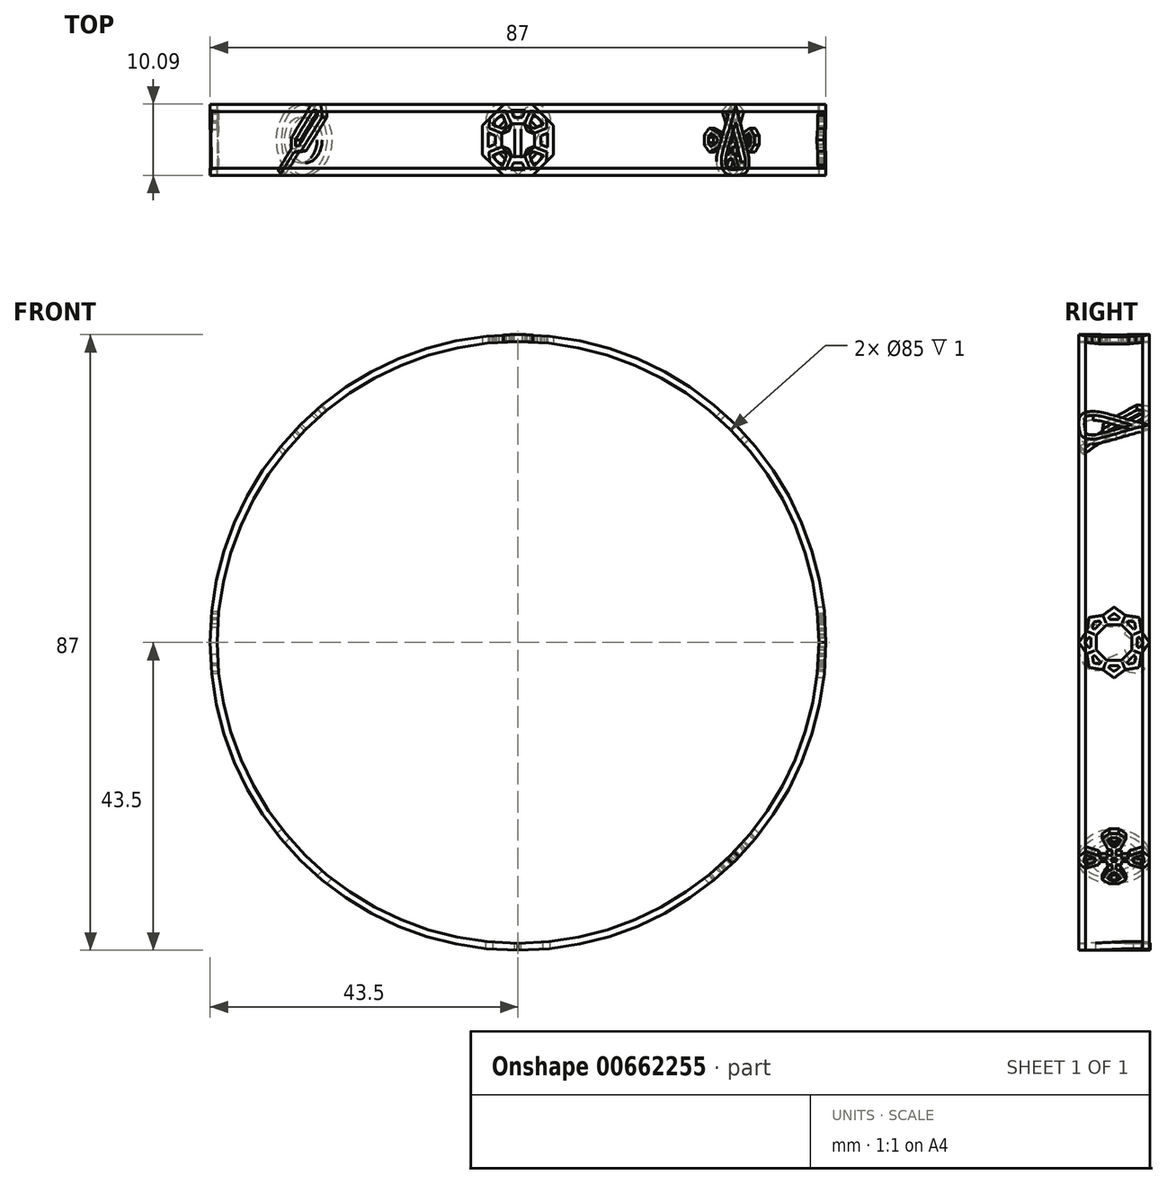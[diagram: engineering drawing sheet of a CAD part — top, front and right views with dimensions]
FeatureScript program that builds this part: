
annotation { "Feature Type Name" : "Feature", "Feature Type Description" : "" }
export const myFeature = defineFeature(function(context is Context, id is Id, definition is map)
    precondition{}
    {
        {
            var Q0;
            Q0=qCreatedBy(makeId("Top.planeOp"),FACE);
            var sketch = newSketch(context, id + "F0", { "sketchPlane" : qUnion([Q0])});
            skCircle(sketch, "E0.cCircle", {"center": v(0, 0) * mm, "radius": 5.41 * mm, "construction": true});
            skLineSegment(sketch, "E0.0", {"start": v(2.07, 5) * mm, "end": v(5, 2.07) * mm});
            skLineSegment(sketch, "E0.1", {"start": v(5, 2.07) * mm, "end": v(5, -2.07) * mm});
            skLineSegment(sketch, "E0.2", {"start": v(5, -2.07) * mm, "end": v(2.07, -5) * mm});
            skLineSegment(sketch, "E0.3", {"start": v(2.07, -5) * mm, "end": v(-2.07, -5) * mm});
            skLineSegment(sketch, "E0.4", {"start": v(-2.07, -5) * mm, "end": v(-5, -2.07) * mm});
            skLineSegment(sketch, "E0.5", {"start": v(-5, -2.07) * mm, "end": v(-5, 2.07) * mm});
            skLineSegment(sketch, "E0.6", {"start": v(-5, 2.07) * mm, "end": v(-2.07, 5) * mm});
            skLineSegment(sketch, "E0.7", {"start": v(-2.07, 5) * mm, "end": v(2.07, 5) * mm});
            skCircle(sketch, "E1.cCircle", {"center": v(0, 0) * mm, "radius": 2.88 * mm, "construction": true});
            skLineSegment(sketch, "E1.0", {"start": v(1.1, 2.66) * mm, "end": v(2.66, 1.1) * mm});
            skLineSegment(sketch, "E1.1", {"start": v(2.66, 1.1) * mm, "end": v(2.66, -1.1) * mm});
            skLineSegment(sketch, "E1.2", {"start": v(2.66, -1.1) * mm, "end": v(1.1, -2.66) * mm});
            skLineSegment(sketch, "E1.3", {"start": v(1.1, -2.66) * mm, "end": v(-1.1, -2.66) * mm});
            skLineSegment(sketch, "E1.4", {"start": v(-1.1, -2.66) * mm, "end": v(-2.66, -1.1) * mm});
            skLineSegment(sketch, "E1.5", {"start": v(-2.66, -1.1) * mm, "end": v(-2.66, 1.1) * mm});
            skLineSegment(sketch, "E1.6", {"start": v(-2.66, 1.1) * mm, "end": v(-1.1, 2.66) * mm});
            skLineSegment(sketch, "E1.7", {"start": v(-1.1, 2.66) * mm, "end": v(1.1, 2.66) * mm});
            skLineSegment(sketch, "E2", {"start": v(-2.07, 5) * mm, "end": v(-1.1, 2.66) * mm});
            skLineSegment(sketch, "E3", {"start": v(-2.66, 1.1) * mm, "end": v(-5, 2.07) * mm});
            skLineSegment(sketch, "E4", {"start": v(-5, -2.07) * mm, "end": v(-2.66, -1.1) * mm});
            skLineSegment(sketch, "E5", {"start": v(-1.1, -2.66) * mm, "end": v(-2.07, -5) * mm});
            skLineSegment(sketch, "E6", {"start": v(1.1, -2.66) * mm, "end": v(2.07, -5) * mm});
            skLineSegment(sketch, "E7", {"start": v(5, -2.07) * mm, "end": v(2.66, -1.1) * mm});
            skLineSegment(sketch, "E8", {"start": v(2.66, 1.1) * mm, "end": v(5, 2.07) * mm});
            skLineSegment(sketch, "E9", {"start": v(2.07, 5) * mm, "end": v(1.1, 2.66) * mm});
            skLineSegment(sketch, "E10", {"start": v(1.03, 4.18) * mm, "end": v(0.62, 3.2) * mm});
            skLineSegment(sketch, "E11", {"start": v(0.62, 3.2) * mm, "end": v(-0.58, 3.2) * mm});
            skLineSegment(sketch, "E12", {"start": v(-0.58, 3.2) * mm, "end": v(-0.98, 4.18) * mm});
            skLineSegment(sketch, "E13", {"start": v(-0.98, 4.18) * mm, "end": v(1.03, 4.18) * mm});
            skLineSegment(sketch, "E14.MirrorCS", {"start": v(2.23, 3.68) * mm, "end": v(1.82, 2.7) * mm});
            skLineSegment(sketch, "E15.MirrorCS", {"start": v(3.65, 2.26) * mm, "end": v(2.23, 3.68) * mm});
            skLineSegment(sketch, "E16.MirrorCS", {"start": v(1.82, 2.7) * mm, "end": v(2.67, 1.85) * mm});
            skLineSegment(sketch, "E17.MirrorCS", {"start": v(2.67, 1.85) * mm, "end": v(3.65, 2.26) * mm});
            skLineSegment(sketch, "E18.MirrorCS", {"start": v(3.2, 0.58) * mm, "end": v(4.18, 0.98) * mm});
            skLineSegment(sketch, "E19.MirrorCS", {"start": v(3.2, -0.62) * mm, "end": v(3.2, 0.58) * mm});
            skLineSegment(sketch, "E20.MirrorCS", {"start": v(4.18, -1.03) * mm, "end": v(3.2, -0.62) * mm});
            skLineSegment(sketch, "E21.MirrorCS", {"start": v(4.18, 0.98) * mm, "end": v(4.18, -1.03) * mm});
            skLineSegment(sketch, "E22.MirrorCS", {"start": v(5, -2.07) * mm, "end": v(5, 2.07) * mm});
            skLineSegment(sketch, "E23.MirrorCS", {"start": v(3.68, -2.23) * mm, "end": v(2.7, -1.82) * mm});
            skLineSegment(sketch, "E24.MirrorCS", {"start": v(2.7, -1.82) * mm, "end": v(1.85, -2.67) * mm});
            skLineSegment(sketch, "E25.MirrorCS", {"start": v(1.85, -2.67) * mm, "end": v(2.26, -3.65) * mm});
            skLineSegment(sketch, "E26.MirrorCS", {"start": v(2.26, -3.65) * mm, "end": v(3.68, -2.23) * mm});
            skLineSegment(sketch, "E27.MirrorCS", {"start": v(0.58, -3.2) * mm, "end": v(0.98, -4.18) * mm});
            skLineSegment(sketch, "E28.MirrorCS", {"start": v(-0.62, -3.2) * mm, "end": v(0.58, -3.2) * mm});
            skLineSegment(sketch, "E29.MirrorCS", {"start": v(0.98, -4.18) * mm, "end": v(-1.03, -4.18) * mm});
            skLineSegment(sketch, "E30.MirrorCS", {"start": v(-1.03, -4.18) * mm, "end": v(-0.62, -3.2) * mm});
            skLineSegment(sketch, "E31.MirrorCS", {"start": v(-2.23, -3.68) * mm, "end": v(-1.82, -2.7) * mm});
            skLineSegment(sketch, "E32.MirrorCS", {"start": v(-1.82, -2.7) * mm, "end": v(-2.67, -1.85) * mm});
            skLineSegment(sketch, "E33.MirrorCS", {"start": v(-2.67, -1.85) * mm, "end": v(-3.65, -2.26) * mm});
            skLineSegment(sketch, "E34.MirrorCS", {"start": v(-3.65, -2.26) * mm, "end": v(-2.23, -3.68) * mm});
            skLineSegment(sketch, "E35.MirrorCS", {"start": v(-3.2, -0.58) * mm, "end": v(-4.18, -0.98) * mm});
            skLineSegment(sketch, "E36.MirrorCS", {"start": v(-2.66, -1.1) * mm, "end": v(-1.1, -2.66) * mm});
            skLineSegment(sketch, "E37.MirrorCS", {"start": v(-3.2, 0.62) * mm, "end": v(-3.2, -0.58) * mm});
            skLineSegment(sketch, "E38.MirrorCS", {"start": v(-4.18, -0.98) * mm, "end": v(-4.18, 1.03) * mm});
            skLineSegment(sketch, "E39.MirrorCS", {"start": v(-4.18, 1.03) * mm, "end": v(-3.2, 0.62) * mm});
            skLineSegment(sketch, "E40.MirrorCS", {"start": v(-3.68, 2.23) * mm, "end": v(-2.7, 1.82) * mm});
            skLineSegment(sketch, "E41.MirrorCS", {"start": v(-2.7, 1.82) * mm, "end": v(-1.85, 2.67) * mm});
            skLineSegment(sketch, "E42.MirrorCS", {"start": v(-1.85, 2.67) * mm, "end": v(-2.26, 3.65) * mm});
            skLineSegment(sketch, "E43.MirrorCS", {"start": v(-2.26, 3.65) * mm, "end": v(-3.68, 2.23) * mm});
            skCircle(sketch, "E44.cCircle", {"center": v(0, 0) * mm, "radius": 2.5 * mm, "construction": true});
            skLineSegment(sketch, "E44.0", {"start": v(0.96, 2.3) * mm, "end": v(2.3, 0.96) * mm});
            skLineSegment(sketch, "E44.1", {"start": v(2.3, 0.96) * mm, "end": v(2.3, -0.96) * mm});
            skLineSegment(sketch, "E44.2", {"start": v(2.3, -0.96) * mm, "end": v(0.96, -2.3) * mm});
            skLineSegment(sketch, "E44.3", {"start": v(0.96, -2.3) * mm, "end": v(-0.96, -2.3) * mm});
            skLineSegment(sketch, "E44.4", {"start": v(-0.96, -2.3) * mm, "end": v(-2.3, -0.96) * mm});
            skLineSegment(sketch, "E44.5", {"start": v(-2.3, -0.96) * mm, "end": v(-2.3, 0.96) * mm});
            skLineSegment(sketch, "E44.6", {"start": v(-2.3, 0.96) * mm, "end": v(-0.96, 2.3) * mm});
            skLineSegment(sketch, "E44.7", {"start": v(-0.96, 2.3) * mm, "end": v(0.96, 2.3) * mm});
            skSolve(sketch);
        }
        {
            var Q0;
            Q0=qCreatedBy(makeId("Top.planeOp"),FACE);
            var sketch = newSketch(context, id + "F1", { "sketchPlane" : qUnion([Q0])});
            skPoint(sketch, "E45", {"position": v(0, 5) * mm});
            skPoint(sketch, "E46", {"position": v(0.02, -5) * mm});
            skFitSpline(sketch, "E47", {"points": [v(0, 5) * mm, v(-2.77, -3.02) * mm], "startDerivative": vector(-3.23, -10.51) * mm, "endDerivative": vector(0.27, -4.22) * mm});
            skFitSpline(sketch, "E48", {"points": [v(-2.77, -3.02) * mm, v(0.02, -5) * mm], "startDerivative": vector(0.37, -5.85) * mm, "endDerivative": vector(4.25, -0.07) * mm});
            skFitSpline(sketch, "E49.MirrorCS", {"points": [v(0, 5) * mm, v(2.77, -3.16) * mm], "startDerivative": vector(3.23, -10.51) * mm, "endDerivative": vector(-0.27, -4.22) * mm});
            skFitSpline(sketch, "E50.MirrorCS", {"points": [v(2.77, -3.16) * mm, v(-0.03, -5) * mm], "startDerivative": vector(-0.37, -5.82) * mm, "endDerivative": vector(-4.2, -0.7) * mm});
            skFitSpline(sketch, "E51.0", {"points": [v(-0.76, 4.76) * mm, v(-0.49, 3.86) * mm, v(0.15, 2.1) * mm, v(0.96, 0.15) * mm, v(1.48, -1.19) * mm, v(1.78, -2.05) * mm, v(1.96, -2.74) * mm, v(1.98, -3.03) * mm, v(1.97, -3.11) * mm]});
            skFitSpline(sketch, "E51.1", {"points": [v(0.76, 4.76) * mm, v(0.49, 3.86) * mm, v(-0.15, 2.12) * mm, v(-0.96, 0.2) * mm, v(-1.48, -1.1) * mm, v(-1.78, -1.94) * mm, v(-1.96, -2.6) * mm, v(-1.98, -2.9) * mm, v(-1.97, -2.97) * mm]});
            skFitSpline(sketch, "E51.2", {"points": [v(-1.97, -2.97) * mm, v(-1.96, -3.18) * mm, v(-1.9, -3.5) * mm, v(-1.79, -3.78) * mm, v(-1.67, -3.92) * mm, v(-1.52, -4.02) * mm, v(-1.28, -4.1) * mm, v(-0.92, -4.16) * mm, v(-0.48, -4.2) * mm, v(-0.14, -4.2) * mm, v(0.04, -4.2) * mm]});
            skFitSpline(sketch, "E51.3", {"points": [v(1.97, -3.11) * mm, v(1.96, -3.31) * mm, v(1.9, -3.62) * mm, v(1.8, -3.83) * mm, v(1.73, -3.9) * mm, v(1.6, -3.98) * mm, v(1.32, -4.05) * mm, v(0.92, -4.1) * mm, v(0.42, -4.14) * mm, v(0.04, -4.18) * mm, v(-0.16, -4.22) * mm]});
            skSolve(sketch);
        }
        {
            var Q0;
            Q0=qCreatedBy(makeId("Top.planeOp"),FACE);
            var sketch = newSketch(context, id + "F2", { "sketchPlane" : qUnion([Q0])});
            skCircle(sketch, "E52.cCircle", {"center": v(0, 0) * mm, "radius": 3 * mm, "construction": true});
            skLineSegment(sketch, "E52.0", {"start": v(1.15, 2.77) * mm, "end": v(2.77, 1.15) * mm});
            skLineSegment(sketch, "E52.1", {"start": v(2.77, 1.15) * mm, "end": v(2.77, -1.15) * mm});
            skLineSegment(sketch, "E52.2", {"start": v(2.77, -1.15) * mm, "end": v(1.15, -2.77) * mm});
            skLineSegment(sketch, "E52.3", {"start": v(1.15, -2.77) * mm, "end": v(-1.15, -2.77) * mm});
            skLineSegment(sketch, "E52.4", {"start": v(-1.15, -2.77) * mm, "end": v(-2.77, -1.15) * mm});
            skLineSegment(sketch, "E52.5", {"start": v(-2.77, -1.15) * mm, "end": v(-2.77, 1.15) * mm});
            skLineSegment(sketch, "E52.6", {"start": v(-2.77, 1.15) * mm, "end": v(-1.15, 2.77) * mm});
            skLineSegment(sketch, "E52.7", {"start": v(-1.15, 2.77) * mm, "end": v(1.15, 2.77) * mm});
            skLineSegment(sketch, "E53", {"start": v(-1.15, 2.77) * mm, "end": v(-1.58, 3.85) * mm});
            skLineSegment(sketch, "E54", {"start": v(-1.58, 3.85) * mm, "end": v(0, 5) * mm});
            skLineSegment(sketch, "E55.MirrorCS", {"start": v(1.58, 3.85) * mm, "end": v(0, 5) * mm});
            skLineSegment(sketch, "E56.MirrorCS", {"start": v(1.15, 2.77) * mm, "end": v(1.58, 3.85) * mm});
            skLineSegment(sketch, "E57.1.0", {"start": v(-1.15, 2.77) * mm, "end": v(-1.6, 3.84) * mm});
            skLineSegment(sketch, "E57.1.1", {"start": v(-1.6, 3.84) * mm, "end": v(-3.54, 3.54) * mm});
            skLineSegment(sketch, "E57.1.2", {"start": v(-3.84, 1.6) * mm, "end": v(-3.54, 3.54) * mm});
            skLineSegment(sketch, "E57.1.3", {"start": v(-2.77, 1.15) * mm, "end": v(-3.84, 1.6) * mm});
            skLineSegment(sketch, "E57.2.0", {"start": v(-2.77, 1.15) * mm, "end": v(-3.85, 1.58) * mm});
            skLineSegment(sketch, "E57.2.1", {"start": v(-3.85, 1.58) * mm, "end": v(-5, 0) * mm});
            skLineSegment(sketch, "E57.2.2", {"start": v(-3.85, -1.58) * mm, "end": v(-5, 0) * mm});
            skLineSegment(sketch, "E57.2.3", {"start": v(-2.77, -1.15) * mm, "end": v(-3.85, -1.58) * mm});
            skLineSegment(sketch, "E57.3.0", {"start": v(-2.77, -1.15) * mm, "end": v(-3.84, -1.6) * mm});
            skLineSegment(sketch, "E57.3.1", {"start": v(-3.84, -1.6) * mm, "end": v(-3.54, -3.54) * mm});
            skLineSegment(sketch, "E57.3.2", {"start": v(-1.6, -3.84) * mm, "end": v(-3.54, -3.54) * mm});
            skLineSegment(sketch, "E57.3.3", {"start": v(-1.15, -2.77) * mm, "end": v(-1.6, -3.84) * mm});
            skLineSegment(sketch, "E57.4.0", {"start": v(-1.15, -2.77) * mm, "end": v(-1.58, -3.85) * mm});
            skLineSegment(sketch, "E57.4.1", {"start": v(-1.58, -3.85) * mm, "end": v(0, -5) * mm});
            skLineSegment(sketch, "E57.4.2", {"start": v(1.58, -3.85) * mm, "end": v(0, -5) * mm});
            skLineSegment(sketch, "E57.4.3", {"start": v(1.15, -2.77) * mm, "end": v(1.58, -3.85) * mm});
            skLineSegment(sketch, "E57.5.0", {"start": v(1.15, -2.77) * mm, "end": v(1.6, -3.84) * mm});
            skLineSegment(sketch, "E57.5.1", {"start": v(1.6, -3.84) * mm, "end": v(3.54, -3.54) * mm});
            skLineSegment(sketch, "E57.5.2", {"start": v(3.84, -1.6) * mm, "end": v(3.54, -3.54) * mm});
            skLineSegment(sketch, "E57.5.3", {"start": v(2.77, -1.15) * mm, "end": v(3.84, -1.6) * mm});
            skLineSegment(sketch, "E57.6.0", {"start": v(2.77, -1.15) * mm, "end": v(3.85, -1.58) * mm});
            skLineSegment(sketch, "E57.6.1", {"start": v(3.85, -1.58) * mm, "end": v(5, 0) * mm});
            skLineSegment(sketch, "E57.6.2", {"start": v(3.85, 1.58) * mm, "end": v(5, 0) * mm});
            skLineSegment(sketch, "E57.6.3", {"start": v(2.77, 1.15) * mm, "end": v(3.85, 1.58) * mm});
            skLineSegment(sketch, "E57.7.0", {"start": v(2.77, 1.15) * mm, "end": v(3.84, 1.6) * mm});
            skLineSegment(sketch, "E57.7.1", {"start": v(3.84, 1.6) * mm, "end": v(3.54, 3.54) * mm});
            skLineSegment(sketch, "E57.7.2", {"start": v(1.6, 3.84) * mm, "end": v(3.54, 3.54) * mm});
            skLineSegment(sketch, "E57.7.3", {"start": v(1.15, 2.77) * mm, "end": v(1.6, 3.84) * mm});
            skLineSegment(sketch, "E58", {"start": v(0, 4.1) * mm, "end": v(-0.73, 3.56) * mm});
            skLineSegment(sketch, "E59", {"start": v(-0.73, 3.56) * mm, "end": v(-0.61, 3.26) * mm});
            skLineSegment(sketch, "E60", {"start": v(-0.61, 3.26) * mm, "end": v(0.62, 3.26) * mm});
            skLineSegment(sketch, "E61", {"start": v(0.62, 3.26) * mm, "end": v(0.74, 3.56) * mm});
            skLineSegment(sketch, "E62", {"start": v(0.74, 3.56) * mm, "end": v(0, 4.1) * mm});
            skCircle(sketch, "E63.cCircle", {"center": v(0, 0) * mm, "radius": 2.73 * mm, "construction": true});
            skLineSegment(sketch, "E63.0", {"start": v(1.05, 2.52) * mm, "end": v(2.52, 1.05) * mm});
            skLineSegment(sketch, "E63.1", {"start": v(2.52, 1.05) * mm, "end": v(2.52, -1.05) * mm});
            skLineSegment(sketch, "E63.2", {"start": v(2.52, -1.05) * mm, "end": v(1.05, -2.52) * mm});
            skLineSegment(sketch, "E63.3", {"start": v(1.05, -2.52) * mm, "end": v(-1.05, -2.52) * mm});
            skLineSegment(sketch, "E63.4", {"start": v(-1.05, -2.52) * mm, "end": v(-2.52, -1.05) * mm});
            skLineSegment(sketch, "E63.5", {"start": v(-2.52, -1.05) * mm, "end": v(-2.52, 1.05) * mm});
            skLineSegment(sketch, "E63.6", {"start": v(-2.52, 1.05) * mm, "end": v(-1.05, 2.52) * mm});
            skLineSegment(sketch, "E63.7", {"start": v(-1.05, 2.52) * mm, "end": v(1.05, 2.52) * mm});
            skLineSegment(sketch, "E64.1.1", {"start": v(-1.87, 2.74) * mm, "end": v(-2, 3.04) * mm});
            skLineSegment(sketch, "E64.1.2", {"start": v(-2.74, 1.87) * mm, "end": v(-1.87, 2.74) * mm});
            skLineSegment(sketch, "E64.1.3", {"start": v(-3.04, 2) * mm, "end": v(-2.74, 1.87) * mm});
            skLineSegment(sketch, "E64.1.4", {"start": v(-2.9, 2.9) * mm, "end": v(-3.04, 2) * mm});
            skLineSegment(sketch, "E64.1.5", {"start": v(-2, 3.04) * mm, "end": v(-2.9, 2.9) * mm});
            skLineSegment(sketch, "E64.2.1", {"start": v(-3.26, 0.62) * mm, "end": v(-3.56, 0.74) * mm});
            skLineSegment(sketch, "E64.2.2", {"start": v(-3.26, -0.61) * mm, "end": v(-3.26, 0.62) * mm});
            skLineSegment(sketch, "E64.2.3", {"start": v(-3.56, -0.73) * mm, "end": v(-3.26, -0.61) * mm});
            skLineSegment(sketch, "E64.2.4", {"start": v(-4.1, 0) * mm, "end": v(-3.56, -0.73) * mm});
            skLineSegment(sketch, "E64.2.5", {"start": v(-3.56, 0.74) * mm, "end": v(-4.1, 0) * mm});
            skLineSegment(sketch, "E64.3.1", {"start": v(-2.74, -1.87) * mm, "end": v(-3.04, -2) * mm});
            skLineSegment(sketch, "E64.3.2", {"start": v(-1.87, -2.74) * mm, "end": v(-2.74, -1.87) * mm});
            skLineSegment(sketch, "E64.3.3", {"start": v(-2, -3.04) * mm, "end": v(-1.87, -2.74) * mm});
            skLineSegment(sketch, "E64.3.4", {"start": v(-2.9, -2.9) * mm, "end": v(-2, -3.04) * mm});
            skLineSegment(sketch, "E64.3.5", {"start": v(-3.04, -2) * mm, "end": v(-2.9, -2.9) * mm});
            skLineSegment(sketch, "E64.4.1", {"start": v(-0.62, -3.26) * mm, "end": v(-0.74, -3.56) * mm});
            skLineSegment(sketch, "E64.4.2", {"start": v(0.61, -3.26) * mm, "end": v(-0.62, -3.26) * mm});
            skLineSegment(sketch, "E64.4.3", {"start": v(0.73, -3.56) * mm, "end": v(0.61, -3.26) * mm});
            skLineSegment(sketch, "E64.4.4", {"start": v(0, -4.1) * mm, "end": v(0.73, -3.56) * mm});
            skLineSegment(sketch, "E64.4.5", {"start": v(-0.74, -3.56) * mm, "end": v(0, -4.1) * mm});
            skLineSegment(sketch, "E64.5.1", {"start": v(1.87, -2.74) * mm, "end": v(2, -3.04) * mm});
            skLineSegment(sketch, "E64.5.2", {"start": v(2.74, -1.87) * mm, "end": v(1.87, -2.74) * mm});
            skLineSegment(sketch, "E64.5.3", {"start": v(3.04, -2) * mm, "end": v(2.74, -1.87) * mm});
            skLineSegment(sketch, "E64.5.4", {"start": v(2.9, -2.9) * mm, "end": v(3.04, -2) * mm});
            skLineSegment(sketch, "E64.5.5", {"start": v(2, -3.04) * mm, "end": v(2.9, -2.9) * mm});
            skLineSegment(sketch, "E64.6.1", {"start": v(3.26, -0.62) * mm, "end": v(3.56, -0.74) * mm});
            skLineSegment(sketch, "E64.6.2", {"start": v(3.26, 0.61) * mm, "end": v(3.26, -0.62) * mm});
            skLineSegment(sketch, "E64.6.3", {"start": v(3.56, 0.73) * mm, "end": v(3.26, 0.61) * mm});
            skLineSegment(sketch, "E64.6.4", {"start": v(4.1, 0) * mm, "end": v(3.56, 0.73) * mm});
            skLineSegment(sketch, "E64.6.5", {"start": v(3.56, -0.74) * mm, "end": v(4.1, 0) * mm});
            skLineSegment(sketch, "E64.7.1", {"start": v(2.74, 1.87) * mm, "end": v(3.04, 2) * mm});
            skLineSegment(sketch, "E64.7.2", {"start": v(1.87, 2.74) * mm, "end": v(2.74, 1.87) * mm});
            skLineSegment(sketch, "E64.7.3", {"start": v(2, 3.04) * mm, "end": v(1.87, 2.74) * mm});
            skLineSegment(sketch, "E64.7.4", {"start": v(2.9, 2.9) * mm, "end": v(2, 3.04) * mm});
            skLineSegment(sketch, "E64.7.5", {"start": v(3.04, 2) * mm, "end": v(2.9, 2.9) * mm});
            skSolve(sketch);
        }
        {
            var Q0;
            Q0=qCreatedBy(makeId("Top.planeOp"),FACE);
            var sketch = newSketch(context, id + "F3", { "sketchPlane" : qUnion([Q0])});
            skLineSegment(sketch, "E65", {"start": v(0.02, 1.79) * mm, "end": v(-0.9, 2.18) * mm});
            skLineSegment(sketch, "E66", {"start": v(-0.9, 2.18) * mm, "end": v(-1.7, 4.1) * mm});
            skLineSegment(sketch, "E67", {"start": v(-1.7, 4.1) * mm, "end": v(-0.65, 5) * mm});
            skLineSegment(sketch, "E68", {"start": v(-0.65, 5) * mm, "end": v(0, 5) * mm});
            skLineSegment(sketch, "E69.MirrorCS", {"start": v(0.65, 5) * mm, "end": v(0, 5) * mm});
            skLineSegment(sketch, "E70.MirrorCS", {"start": v(1.7, 4.1) * mm, "end": v(0.65, 5) * mm});
            skLineSegment(sketch, "E71.MirrorCS", {"start": v(0.9, 2.18) * mm, "end": v(1.7, 4.1) * mm});
            skLineSegment(sketch, "E72.MirrorCS", {"start": v(-0.02, 1.79) * mm, "end": v(0.9, 2.18) * mm});
            skLineSegment(sketch, "E73.1.0", {"start": v(-2.18, 0.9) * mm, "end": v(-4.09, 1.7) * mm});
            skLineSegment(sketch, "E73.1.1", {"start": v(-4.09, 1.7) * mm, "end": v(-4, 3.07) * mm});
            skLineSegment(sketch, "E73.1.2", {"start": v(-4, 3.07) * mm, "end": v(-3.54, 3.54) * mm});
            skLineSegment(sketch, "E73.1.3", {"start": v(-1.25, 1.28) * mm, "end": v(-2.18, 0.9) * mm});
            skLineSegment(sketch, "E73.1.4", {"start": v(-3.07, 4) * mm, "end": v(-3.54, 3.54) * mm});
            skLineSegment(sketch, "E73.1.5", {"start": v(-1.7, 4.09) * mm, "end": v(-3.07, 4) * mm});
            skLineSegment(sketch, "E73.1.6", {"start": v(-0.9, 2.18) * mm, "end": v(-1.7, 4.09) * mm});
            skLineSegment(sketch, "E73.1.7", {"start": v(-1.28, 1.25) * mm, "end": v(-0.9, 2.18) * mm});
            skLineSegment(sketch, "E73.2.0", {"start": v(-2.18, -0.9) * mm, "end": v(-4.1, -1.7) * mm});
            skLineSegment(sketch, "E73.2.1", {"start": v(-4.1, -1.7) * mm, "end": v(-5, -0.65) * mm});
            skLineSegment(sketch, "E73.2.2", {"start": v(-5, -0.65) * mm, "end": v(-5, 0) * mm});
            skLineSegment(sketch, "E73.2.3", {"start": v(-1.79, 0.02) * mm, "end": v(-2.18, -0.9) * mm});
            skLineSegment(sketch, "E73.2.4", {"start": v(-5, 0.65) * mm, "end": v(-5, 0) * mm});
            skLineSegment(sketch, "E73.2.5", {"start": v(-4.1, 1.7) * mm, "end": v(-5, 0.65) * mm});
            skLineSegment(sketch, "E73.2.6", {"start": v(-2.18, 0.9) * mm, "end": v(-4.1, 1.7) * mm});
            skLineSegment(sketch, "E73.2.7", {"start": v(-1.79, -0.02) * mm, "end": v(-2.18, 0.9) * mm});
            skLineSegment(sketch, "E73.3.0", {"start": v(-0.9, -2.18) * mm, "end": v(-1.7, -4.09) * mm});
            skLineSegment(sketch, "E73.3.1", {"start": v(-1.7, -4.09) * mm, "end": v(-3.07, -4) * mm});
            skLineSegment(sketch, "E73.3.2", {"start": v(-3.07, -4) * mm, "end": v(-3.54, -3.54) * mm});
            skLineSegment(sketch, "E73.3.3", {"start": v(-1.28, -1.25) * mm, "end": v(-0.9, -2.18) * mm});
            skLineSegment(sketch, "E73.3.4", {"start": v(-4, -3.07) * mm, "end": v(-3.54, -3.54) * mm});
            skLineSegment(sketch, "E73.3.5", {"start": v(-4.09, -1.7) * mm, "end": v(-4, -3.07) * mm});
            skLineSegment(sketch, "E73.3.6", {"start": v(-2.18, -0.9) * mm, "end": v(-4.09, -1.7) * mm});
            skLineSegment(sketch, "E73.3.7", {"start": v(-1.25, -1.28) * mm, "end": v(-2.18, -0.9) * mm});
            skLineSegment(sketch, "E73.4.0", {"start": v(0.9, -2.18) * mm, "end": v(1.7, -4.1) * mm});
            skLineSegment(sketch, "E73.4.1", {"start": v(1.7, -4.1) * mm, "end": v(0.65, -5) * mm});
            skLineSegment(sketch, "E73.4.2", {"start": v(0.65, -5) * mm, "end": v(0, -5) * mm});
            skLineSegment(sketch, "E73.4.3", {"start": v(-0.02, -1.79) * mm, "end": v(0.9, -2.18) * mm});
            skLineSegment(sketch, "E73.4.4", {"start": v(-0.65, -5) * mm, "end": v(0, -5) * mm});
            skLineSegment(sketch, "E73.4.5", {"start": v(-1.7, -4.1) * mm, "end": v(-0.65, -5) * mm});
            skLineSegment(sketch, "E73.4.6", {"start": v(-0.9, -2.18) * mm, "end": v(-1.7, -4.1) * mm});
            skLineSegment(sketch, "E73.4.7", {"start": v(0.02, -1.79) * mm, "end": v(-0.9, -2.18) * mm});
            skLineSegment(sketch, "E73.5.0", {"start": v(2.18, -0.9) * mm, "end": v(4.09, -1.7) * mm});
            skLineSegment(sketch, "E73.5.1", {"start": v(4.09, -1.7) * mm, "end": v(4, -3.07) * mm});
            skLineSegment(sketch, "E73.5.2", {"start": v(4, -3.07) * mm, "end": v(3.54, -3.54) * mm});
            skLineSegment(sketch, "E73.5.3", {"start": v(1.25, -1.28) * mm, "end": v(2.18, -0.9) * mm});
            skLineSegment(sketch, "E73.5.4", {"start": v(3.07, -4) * mm, "end": v(3.54, -3.54) * mm});
            skLineSegment(sketch, "E73.5.5", {"start": v(1.7, -4.09) * mm, "end": v(3.07, -4) * mm});
            skLineSegment(sketch, "E73.5.6", {"start": v(0.9, -2.18) * mm, "end": v(1.7, -4.09) * mm});
            skLineSegment(sketch, "E73.5.7", {"start": v(1.28, -1.25) * mm, "end": v(0.9, -2.18) * mm});
            skLineSegment(sketch, "E73.6.0", {"start": v(2.18, 0.9) * mm, "end": v(4.1, 1.7) * mm});
            skLineSegment(sketch, "E73.6.1", {"start": v(4.1, 1.7) * mm, "end": v(5, 0.65) * mm});
            skLineSegment(sketch, "E73.6.2", {"start": v(5, 0.65) * mm, "end": v(5, 0) * mm});
            skLineSegment(sketch, "E73.6.3", {"start": v(1.79, -0.02) * mm, "end": v(2.18, 0.9) * mm});
            skLineSegment(sketch, "E73.6.4", {"start": v(5, -0.65) * mm, "end": v(5, 0) * mm});
            skLineSegment(sketch, "E73.6.5", {"start": v(4.1, -1.7) * mm, "end": v(5, -0.65) * mm});
            skLineSegment(sketch, "E73.6.6", {"start": v(2.18, -0.9) * mm, "end": v(4.1, -1.7) * mm});
            skLineSegment(sketch, "E73.6.7", {"start": v(1.79, 0.02) * mm, "end": v(2.18, -0.9) * mm});
            skLineSegment(sketch, "E73.7.0", {"start": v(0.9, 2.18) * mm, "end": v(1.7, 4.09) * mm});
            skLineSegment(sketch, "E73.7.1", {"start": v(1.7, 4.09) * mm, "end": v(3.07, 4) * mm});
            skLineSegment(sketch, "E73.7.2", {"start": v(3.07, 4) * mm, "end": v(3.54, 3.54) * mm});
            skLineSegment(sketch, "E73.7.3", {"start": v(1.28, 1.25) * mm, "end": v(0.9, 2.18) * mm});
            skLineSegment(sketch, "E73.7.4", {"start": v(4, 3.07) * mm, "end": v(3.54, 3.54) * mm});
            skLineSegment(sketch, "E73.7.5", {"start": v(4.09, 1.7) * mm, "end": v(4, 3.07) * mm});
            skLineSegment(sketch, "E73.7.6", {"start": v(2.18, 0.9) * mm, "end": v(4.09, 1.7) * mm});
            skLineSegment(sketch, "E73.7.7", {"start": v(1.25, 1.28) * mm, "end": v(2.18, 0.9) * mm});
            skPoint(sketch, "E73.center", {"position": v(0, 0) * mm});
            skLineSegment(sketch, "E74.anchor1", {"start": v(0, 0) * mm, "end": v(0.78, 2.7) * mm, "construction": true});
            skLineSegment(sketch, "E74.anchor2", {"start": v(0, 0) * mm, "end": v(-1.35, 2.46) * mm, "construction": true});
            skLineSegment(sketch, "E75.bottom", {"start": v(0.97, 1.02) * mm, "end": v(-0.97, 1.02) * mm});
            skLineSegment(sketch, "E75.top", {"start": v(0.97, -1.02) * mm, "end": v(-0.97, -1.02) * mm});
            skLineSegment(sketch, "E75.left", {"start": v(0.97, 1.02) * mm, "end": v(0.97, -1.02) * mm});
            skLineSegment(sketch, "E75.right", {"start": v(-0.97, 1.02) * mm, "end": v(-0.97, -1.02) * mm});
            skLineSegment(sketch, "E76", {"start": v(-0.3, 1.93) * mm, "end": v(-0.3, 1.02) * mm});
            skLineSegment(sketch, "E77", {"start": v(0.3, 1.93) * mm, "end": v(0.3, 1.02) * mm});
            skLineSegment(sketch, "E78", {"start": v(0.3, 1.02) * mm, "end": v(0.32, 0.96) * mm});
            skLineSegment(sketch, "E79.MirrorCS", {"start": v(0.3, -1.93) * mm, "end": v(0.3, -1.02) * mm});
            skLineSegment(sketch, "E80.MirrorCS", {"start": v(-0.3, -1.93) * mm, "end": v(-0.3, -1.02) * mm});
            skLineSegment(sketch, "E81", {"start": v(-0.97, 0.3) * mm, "end": v(-1.93, 0.3) * mm});
            skLineSegment(sketch, "E82", {"start": v(-0.97, -0.3) * mm, "end": v(-1.93, -0.3) * mm});
            skLineSegment(sketch, "E83.MirrorCS", {"start": v(0.97, 0.3) * mm, "end": v(1.93, 0.3) * mm});
            skLineSegment(sketch, "E84.MirrorCS", {"start": v(0.97, -0.3) * mm, "end": v(1.93, -0.3) * mm});
            skLineSegment(sketch, "E85", {"start": v(0, 2.58) * mm, "end": v(-0.43, 2.79) * mm});
            skLineSegment(sketch, "E86", {"start": v(-0.43, 2.79) * mm, "end": v(-0.92, 3.84) * mm});
            skLineSegment(sketch, "E87", {"start": v(-0.92, 3.84) * mm, "end": v(-0.39, 4.23) * mm});
            skLineSegment(sketch, "E88", {"start": v(-0.39, 4.23) * mm, "end": v(0, 4.23) * mm});
            skLineSegment(sketch, "E89.MirrorCS", {"start": v(0.39, 4.23) * mm, "end": v(0, 4.23) * mm});
            skLineSegment(sketch, "E90.MirrorCS", {"start": v(0.92, 3.84) * mm, "end": v(0.39, 4.23) * mm});
            skLineSegment(sketch, "E91.MirrorCS", {"start": v(0.43, 2.79) * mm, "end": v(0.92, 3.84) * mm});
            skLineSegment(sketch, "E92.MirrorCS", {"start": v(0, 2.58) * mm, "end": v(0.43, 2.79) * mm});
            skLineSegment(sketch, "E93.1.0", {"start": v(-2.71, 3.26) * mm, "end": v(-2.99, 2.99) * mm});
            skLineSegment(sketch, "E93.1.1", {"start": v(-3.26, 2.71) * mm, "end": v(-2.99, 2.99) * mm});
            skLineSegment(sketch, "E93.1.2", {"start": v(-3.37, 2.07) * mm, "end": v(-3.26, 2.71) * mm});
            skLineSegment(sketch, "E93.1.3", {"start": v(-2.28, 1.66) * mm, "end": v(-3.37, 2.07) * mm});
            skLineSegment(sketch, "E93.1.4", {"start": v(-1.82, 1.82) * mm, "end": v(-2.28, 1.66) * mm});
            skLineSegment(sketch, "E93.1.5", {"start": v(-1.82, 1.82) * mm, "end": v(-1.66, 2.28) * mm});
            skLineSegment(sketch, "E93.1.6", {"start": v(-1.66, 2.28) * mm, "end": v(-2.07, 3.37) * mm});
            skLineSegment(sketch, "E93.1.7", {"start": v(-2.07, 3.37) * mm, "end": v(-2.71, 3.26) * mm});
            skLineSegment(sketch, "E93.2.0", {"start": v(-4.23, 0.39) * mm, "end": v(-4.23, 0) * mm});
            skLineSegment(sketch, "E93.2.1", {"start": v(-4.23, -0.39) * mm, "end": v(-4.23, 0) * mm});
            skLineSegment(sketch, "E93.2.2", {"start": v(-3.84, -0.92) * mm, "end": v(-4.23, -0.39) * mm});
            skLineSegment(sketch, "E93.2.3", {"start": v(-2.79, -0.43) * mm, "end": v(-3.84, -0.92) * mm});
            skLineSegment(sketch, "E93.2.4", {"start": v(-2.58, 0) * mm, "end": v(-2.79, -0.43) * mm});
            skLineSegment(sketch, "E93.2.5", {"start": v(-2.58, 0) * mm, "end": v(-2.79, 0.43) * mm});
            skLineSegment(sketch, "E93.2.6", {"start": v(-2.79, 0.43) * mm, "end": v(-3.84, 0.92) * mm});
            skLineSegment(sketch, "E93.2.7", {"start": v(-3.84, 0.92) * mm, "end": v(-4.23, 0.39) * mm});
            skLineSegment(sketch, "E93.3.0", {"start": v(-3.26, -2.71) * mm, "end": v(-2.99, -2.99) * mm});
            skLineSegment(sketch, "E93.3.1", {"start": v(-2.71, -3.26) * mm, "end": v(-2.99, -2.99) * mm});
            skLineSegment(sketch, "E93.3.2", {"start": v(-2.07, -3.37) * mm, "end": v(-2.71, -3.26) * mm});
            skLineSegment(sketch, "E93.3.3", {"start": v(-1.66, -2.28) * mm, "end": v(-2.07, -3.37) * mm});
            skLineSegment(sketch, "E93.3.4", {"start": v(-1.82, -1.82) * mm, "end": v(-1.66, -2.28) * mm});
            skLineSegment(sketch, "E93.3.5", {"start": v(-1.82, -1.82) * mm, "end": v(-2.28, -1.66) * mm});
            skLineSegment(sketch, "E93.3.6", {"start": v(-2.28, -1.66) * mm, "end": v(-3.37, -2.07) * mm});
            skLineSegment(sketch, "E93.3.7", {"start": v(-3.37, -2.07) * mm, "end": v(-3.26, -2.71) * mm});
            skLineSegment(sketch, "E93.4.0", {"start": v(-0.39, -4.23) * mm, "end": v(0, -4.23) * mm});
            skLineSegment(sketch, "E93.4.1", {"start": v(0.39, -4.23) * mm, "end": v(0, -4.23) * mm});
            skLineSegment(sketch, "E93.4.2", {"start": v(0.92, -3.84) * mm, "end": v(0.39, -4.23) * mm});
            skLineSegment(sketch, "E93.4.3", {"start": v(0.43, -2.79) * mm, "end": v(0.92, -3.84) * mm});
            skLineSegment(sketch, "E93.4.4", {"start": v(0, -2.58) * mm, "end": v(0.43, -2.79) * mm});
            skLineSegment(sketch, "E93.4.5", {"start": v(0, -2.58) * mm, "end": v(-0.43, -2.79) * mm});
            skLineSegment(sketch, "E93.4.6", {"start": v(-0.43, -2.79) * mm, "end": v(-0.92, -3.84) * mm});
            skLineSegment(sketch, "E93.4.7", {"start": v(-0.92, -3.84) * mm, "end": v(-0.39, -4.23) * mm});
            skLineSegment(sketch, "E93.5.0", {"start": v(2.71, -3.26) * mm, "end": v(2.99, -2.99) * mm});
            skLineSegment(sketch, "E93.5.1", {"start": v(3.26, -2.71) * mm, "end": v(2.99, -2.99) * mm});
            skLineSegment(sketch, "E93.5.2", {"start": v(3.37, -2.07) * mm, "end": v(3.26, -2.71) * mm});
            skLineSegment(sketch, "E93.5.3", {"start": v(2.28, -1.66) * mm, "end": v(3.37, -2.07) * mm});
            skLineSegment(sketch, "E93.5.4", {"start": v(1.82, -1.82) * mm, "end": v(2.28, -1.66) * mm});
            skLineSegment(sketch, "E93.5.5", {"start": v(1.82, -1.82) * mm, "end": v(1.66, -2.28) * mm});
            skLineSegment(sketch, "E93.5.6", {"start": v(1.66, -2.28) * mm, "end": v(2.07, -3.37) * mm});
            skLineSegment(sketch, "E93.5.7", {"start": v(2.07, -3.37) * mm, "end": v(2.71, -3.26) * mm});
            skLineSegment(sketch, "E93.6.0", {"start": v(4.23, -0.39) * mm, "end": v(4.23, 0) * mm});
            skLineSegment(sketch, "E93.6.1", {"start": v(4.23, 0.39) * mm, "end": v(4.23, 0) * mm});
            skLineSegment(sketch, "E93.6.2", {"start": v(3.84, 0.92) * mm, "end": v(4.23, 0.39) * mm});
            skLineSegment(sketch, "E93.6.3", {"start": v(2.79, 0.43) * mm, "end": v(3.84, 0.92) * mm});
            skLineSegment(sketch, "E93.6.4", {"start": v(2.58, 0) * mm, "end": v(2.79, 0.43) * mm});
            skLineSegment(sketch, "E93.6.5", {"start": v(2.58, 0) * mm, "end": v(2.79, -0.43) * mm});
            skLineSegment(sketch, "E93.6.6", {"start": v(2.79, -0.43) * mm, "end": v(3.84, -0.92) * mm});
            skLineSegment(sketch, "E93.6.7", {"start": v(3.84, -0.92) * mm, "end": v(4.23, -0.39) * mm});
            skLineSegment(sketch, "E93.7.0", {"start": v(3.26, 2.71) * mm, "end": v(2.99, 2.99) * mm});
            skLineSegment(sketch, "E93.7.1", {"start": v(2.71, 3.26) * mm, "end": v(2.99, 2.99) * mm});
            skLineSegment(sketch, "E93.7.2", {"start": v(2.07, 3.37) * mm, "end": v(2.71, 3.26) * mm});
            skLineSegment(sketch, "E93.7.3", {"start": v(1.66, 2.28) * mm, "end": v(2.07, 3.37) * mm});
            skLineSegment(sketch, "E93.7.4", {"start": v(1.82, 1.82) * mm, "end": v(1.66, 2.28) * mm});
            skLineSegment(sketch, "E93.7.5", {"start": v(1.82, 1.82) * mm, "end": v(2.28, 1.66) * mm});
            skLineSegment(sketch, "E93.7.6", {"start": v(2.28, 1.66) * mm, "end": v(3.37, 2.07) * mm});
            skLineSegment(sketch, "E93.7.7", {"start": v(3.37, 2.07) * mm, "end": v(3.26, 2.71) * mm});
            skLineSegment(sketch, "E94.0", {"start": v(0.32, 0.37) * mm, "end": v(-0.32, 0.37) * mm});
            skLineSegment(sketch, "E94.1", {"start": v(0.32, 0.37) * mm, "end": v(0.32, -0.37) * mm});
            skLineSegment(sketch, "E94.2", {"start": v(0.32, -0.37) * mm, "end": v(-0.32, -0.37) * mm});
            skLineSegment(sketch, "E94.3", {"start": v(-0.32, 0.37) * mm, "end": v(-0.32, -0.37) * mm});
            skSolve(sketch);
        }
        {
            var Q0;
            Q0=qCreatedBy(makeId("Top.planeOp"),FACE);
            var sketch = newSketch(context, id + "F4", { "sketchPlane" : qUnion([Q0])});
            skPoint(sketch, "E95.0", {"position": v(0, -5) * mm});
            skPoint(sketch, "E96.0", {"position": v(0, 5) * mm});
            skFitSpline(sketch, "E97", {"points": [v(0, 2.76) * mm, v(-2.3, 5.09) * mm, v(-4.53, 3.13) * mm, v(0, -5) * mm], "startDerivative": vector(-5.61, 12.06) * mm, "endDerivative": vector(15.54, -19.43) * mm});
            skLineSegment(sketch, "E98", {"start": v(-0.44, 3.58) * mm, "end": v(-0.44, -4.45) * mm});
            skLineSegment(sketch, "E99", {"start": v(0, 2.76) * mm, "end": v(0, -5) * mm});
            skFitSpline(sketch, "E100", {"points": [v(-0.44, 1.52) * mm, v(-1.53, 3.43) * mm, v(-2.87, 3.8) * mm, v(-3.5, 2.76) * mm, v(-2.68, 0.31) * mm, v(-1.37, -1.51) * mm, v(-0.44, -2.57) * mm], "startDerivative": vector(0, 7.67) * mm, "endDerivative": vector(7.35, -8.63) * mm});
            skFitSpline(sketch, "E101.MirrorCS", {"points": [v(0.44, 1.52) * mm, v(1.53, 3.43) * mm, v(2.87, 3.8) * mm, v(3.5, 2.76) * mm, v(2.68, 0.31) * mm, v(1.37, -1.51) * mm, v(0.44, -2.57) * mm], "startDerivative": vector(0, 7.67) * mm, "endDerivative": vector(-7.35, -8.63) * mm});
            skLineSegment(sketch, "E102.MirrorCS", {"start": v(0.44, 3.58) * mm, "end": v(0.44, -4.45) * mm});
            skFitSpline(sketch, "E103.MirrorCS", {"points": [v(0, 2.76) * mm, v(2.3, 5.09) * mm, v(4.53, 3.13) * mm, v(0, -5) * mm], "startDerivative": vector(5.61, 12.06) * mm, "endDerivative": vector(-15.54, -19.43) * mm});
            skSolve(sketch);
        }
        {
            var Q0;
            Q0=qCreatedBy(makeId("Top.planeOp"),FACE);
            var sketch = newSketch(context, id + "F5", { "sketchPlane" : qUnion([Q0])});
            skCircle(sketch, "E104", {"center": v(0, 0) * mm, "radius": 5 * mm});
            skCircle(sketch, "E105", {"center": v(0, 0) * mm, "radius": 3.25 * mm});
            skSolve(sketch);
        }
        {
            var Q0;
            Q0=qCreatedBy(makeId("Top.planeOp"),FACE);
            var sketch = newSketch(context, id + "F6", { "sketchPlane" : qUnion([Q0])});
            skPoint(sketch, "E106", {"position": v(0, 5) * mm});
            skFitSpline(sketch, "E107", {"points": [v(0, 5) * mm, v(-1.13, 3.67) * mm, v(-1.6, 2.67) * mm, v(-3.92, 4.28) * mm, v(-4.07, 1.76) * mm, v(-3.21, 0.32) * mm, v(-3.95, -1.98) * mm, v(-3.65, -3.76) * mm, v(0, -5) * mm], "startDerivative": vector(-11.46, -12.89) * mm, "endDerivative": vector(30.36, 0) * mm});
            skFitSpline(sketch, "E108.MirrorCS", {"points": [v(0, 5) * mm, v(1.13, 3.67) * mm, v(1.6, 2.67) * mm, v(3.92, 4.28) * mm, v(4.07, 1.76) * mm, v(3.21, 0.32) * mm, v(3.95, -1.98) * mm, v(3.65, -3.76) * mm, v(0, -5) * mm], "startDerivative": vector(11.46, -12.89) * mm, "endDerivative": vector(-30.36, 0) * mm});
            skPoint(sketch, "E109", {"position": v(0, 3.63) * mm});
            skFitSpline(sketch, "E110", {"points": [v(0, 3.63) * mm, v(-0.42, 2.87) * mm, v(-1, 1.48) * mm, v(-3.07, 2.38) * mm, v(-3.02, 1.6) * mm, v(-1.74, 0.74) * mm, v(-2.04, -0.5) * mm, v(-2.8, -2.04) * mm, v(-2.88, -3.3) * mm, v(-1.05, -4.13) * mm, v(1.64, -3.92) * mm, v(2.63, -2.85) * mm, v(2.15, 0.27) * mm, v(2.8, 1.38) * mm, v(3.44, 2.66) * mm, v(1.9, 1.5) * mm, v(0.6, 2.13) * mm, v(0, 3.63) * mm]});
            skSolve(sketch);
        }
        {
            var Q0;
            Q0=qCreatedBy(makeId("Top.planeOp"),FACE);
            var sketch = newSketch(context, id + "F7", { "sketchPlane" : qUnion([Q0])});
            skLineSegment(sketch, "E111", {"start": v(-4.1, -4.8) * mm, "end": v(-4.65, -4.3) * mm});
            skLineSegment(sketch, "E112", {"start": v(-4.65, -4.3) * mm, "end": v(-1.8, -1.18) * mm});
            skLineSegment(sketch, "E113", {"start": v(-1.8, -1.18) * mm, "end": v(-1.8, 0.3) * mm});
            skLineSegment(sketch, "E114", {"start": v(-1.8, 0.3) * mm, "end": v(2.15, 5) * mm});
            skLineSegment(sketch, "E115", {"start": v(2.15, 5) * mm, "end": v(3.96, 5) * mm});
            skLineSegment(sketch, "E116", {"start": v(-4.1, -4.8) * mm, "end": v(-1.25, -1.7) * mm});
            skLineSegment(sketch, "E117", {"start": v(-1.25, -1.7) * mm, "end": v(0.22, -1.52) * mm});
            skLineSegment(sketch, "E118", {"start": v(0.22, -1.52) * mm, "end": v(4.15, 3.2) * mm});
            skLineSegment(sketch, "E119", {"start": v(4.15, 3.2) * mm, "end": v(3.96, 5) * mm});
            skLineSegment(sketch, "E120.0", {"start": v(-1, -0.86) * mm, "end": v(-0.2, -0.76) * mm});
            skLineSegment(sketch, "E120.1", {"start": v(-0.2, -0.76) * mm, "end": v(3.32, 3.46) * mm});
            skLineSegment(sketch, "E120.2", {"start": v(-1, -0.86) * mm, "end": v(-1, 0) * mm});
            skLineSegment(sketch, "E120.3", {"start": v(-1, 0) * mm, "end": v(2.53, 4.2) * mm});
            skLineSegment(sketch, "E120.4", {"start": v(2.53, 4.2) * mm, "end": v(3.24, 4.2) * mm});
            skLineSegment(sketch, "E120.5", {"start": v(3.32, 3.46) * mm, "end": v(3.24, 4.2) * mm});
            skSolve(sketch);
        }
        {
            var Q0;
            Q0=qCreatedBy(makeId("Top.planeOp"),FACE);
            var sketch = newSketch(context, id + "F8", { "sketchPlane" : qUnion([Q0])});
            skCircle(sketch, "E121.cCircle", {"center": v(43, 4.5) * mm, "radius": 0.7 * mm, "construction": true});
            skLineSegment(sketch, "E121.1", {"start": v(42.5, 4) * mm, "end": v(42.5, 5) * mm});
            skLineSegment(sketch, "E121.3", {"start": v(43.5, 5) * mm, "end": v(43.5, 4) * mm});
            skLineSegment(sketch, "E122.MirrorCS", {"start": v(42.5, -4) * mm, "end": v(42.5, -5) * mm});
            skLineSegment(sketch, "E123.MirrorCS", {"start": v(43.5, -5) * mm, "end": v(43.5, -4) * mm});
            skLineSegment(sketch, "E124", {"start": v(0, 62.61) * mm, "end": v(0, -51.25) * mm});
            skLineSegment(sketch, "E125", {"start": v(42.5, -7.23) * mm, "end": v(42.5, 7.7) * mm});
            skLineSegment(sketch, "E126", {"start": v(42.5, 7.7) * mm, "end": v(0, 7.7) * mm});
            skLineSegment(sketch, "E127", {"start": v(42.5, -7.23) * mm, "end": v(0, -7.23) * mm});
            skLineSegment(sketch, "E128", {"start": v(0, -7.23) * mm, "end": v(0, 7.7) * mm});
            skLineSegment(sketch, "E129", {"start": v(43.5, -7.23) * mm, "end": v(43.5, 7.7) * mm});
            skLineSegment(sketch, "E130", {"start": v(43.5, 7.7) * mm, "end": v(156.87, 7.7) * mm});
            skLineSegment(sketch, "E131", {"start": v(156.87, 7.7) * mm, "end": v(156.87, -7.23) * mm});
            skLineSegment(sketch, "E132", {"start": v(156.87, -7.23) * mm, "end": v(43.5, -7.23) * mm});
            skLineSegment(sketch, "E133", {"start": v(43.5, 5) * mm, "end": v(42.5, 5) * mm});
            skLineSegment(sketch, "E134", {"start": v(43.5, 4) * mm, "end": v(42.5, 4) * mm});
            skLineSegment(sketch, "E135", {"start": v(43.5, -4) * mm, "end": v(42.5, -4) * mm});
            skLineSegment(sketch, "E136", {"start": v(43.5, -5) * mm, "end": v(42.5, -5) * mm});
            skSolve(sketch);
        }
        {
            var Q0;
            Q0=makeQuery(id+"F0.imprint","IMPRINT",FACE,{"disambiguationData":[TD([[makeQuery(id+"F0.imprint","IMPRINT",EDGE,{"derivedFrom":sQuery(id+"F0.wireOp",EDGE,"E0.6")}),-1.0]])]});
            var Q1;
            Q1=makeQuery(id+"F0.imprint","IMPRINT",FACE,{"disambiguationData":[TD([[makeQuery(id+"F0.imprint","IMPRINT",EDGE,{"derivedFrom":sQuery(id+"F0.wireOp",EDGE,"E1.0")}),-1.0]])]});
            var Q2;
            Q2=makeQuery(id+"F0.imprint","IMPRINT",FACE,{"disambiguationData":[TD([[makeQuery(id+"F0.imprint","IMPRINT",EDGE,{"derivedFrom":sQuery(id+"F0.wireOp",EDGE,"E0.5")}),-1.0]])]});
            var Q3;
            Q3=makeQuery(id+"F0.imprint","IMPRINT",FACE,{"disambiguationData":[TD([[makeQuery(id+"F0.imprint","IMPRINT",EDGE,{"derivedFrom":sQuery(id+"F0.wireOp",EDGE,"E0.4")}),-1.0]])]});
            var Q4;
            Q4=makeQuery(id+"F0.imprint","IMPRINT",FACE,{"disambiguationData":[TD([[makeQuery(id+"F0.imprint","IMPRINT",EDGE,{"derivedFrom":sQuery(id+"F0.wireOp",EDGE,"E0.3")}),-1.0]])]});
            var Q5;
            Q5=makeQuery(id+"F0.imprint","IMPRINT",FACE,{"disambiguationData":[TD([[makeQuery(id+"F0.imprint","IMPRINT",EDGE,{"derivedFrom":sQuery(id+"F0.wireOp",EDGE,"E0.2")}),-1.0]])]});
            var Q6;
            Q6=makeQuery(id+"F0.imprint","IMPRINT",FACE,{"disambiguationData":[TD([[makeQuery(id+"F0.imprint","IMPRINT",EDGE,{"derivedFrom":sQuery(id+"F0.wireOp",EDGE,"E1.1")}),1.0]])]});
            var Q7;
            Q7=makeQuery(id+"F0.imprint","IMPRINT",FACE,{"disambiguationData":[TD([[makeQuery(id+"F0.imprint","IMPRINT",EDGE,{"derivedFrom":sQuery(id+"F0.wireOp",EDGE,"E0.0")}),-1.0]])]});
            var Q8;
            Q8=makeQuery(id+"F0.imprint","IMPRINT",FACE,{"disambiguationData":[TD([[makeQuery(id+"F0.imprint","IMPRINT",EDGE,{"derivedFrom":sQuery(id+"F0.wireOp",EDGE,"E0.7")}),-1.0]])]});
            extrude(context, id + "F9", {"entities" : qUnion([Q0, Q1, Q2, Q3, Q4, Q5, Q6, Q7, Q8]), "depth" : 100 * mm, "offsetDistance" : 25 * mm});
        }
        {
            var Q0;
            Q0 = qSketchRegion(id + "F1", true);
            extrude(context, id + "F10", {"entities" : qUnion([Q0]), "depth" : 100 * mm, "offsetDistance" : 25 * mm});
        }
        {
            var Q0;
            Q0=makeQuery(id+"F10.opExtrude","SWEPT_BODY",BODY,{"disambiguationData":[OSD([sQuery(id+"F1.wireOp",EDGE,"E47"),sQuery(id+"F1.wireOp",EDGE,"E48"),sQuery(id+"F1.wireOp",EDGE,"E49.MirrorCS"),sQuery(id+"F1.wireOp",EDGE,"E50.MirrorCS"),sQuery(id+"F1.wireOp",EDGE,"E51.0"),sQuery(id+"F1.wireOp",EDGE,"E51.1"),sQuery(id+"F1.wireOp",EDGE,"E51.2"),sQuery(id+"F1.wireOp",EDGE,"E51.3")])]});
            var Q1;
            Q1=sQuery(id+"F8.wireOp",EDGE,"E124");
            transform(context, id + "F11", {"entities" : qUnion([Q0]), "transformType" : TransformType.ROTATION, "transformAxis" : qUnion([Q1]), "angle" : 45 * degree, "oppositeDirection" : true, "makeCopy" : false});
        }
        {
            var Q0;
            Q0 = qSketchRegion(id + "F2", true);
            extrude(context, id + "F12", {"entities" : qUnion([Q0]), "depth" : 100 * mm, "offsetDistance" : 25 * mm});
        }
        {
            var Q0;
            Q0=makeQuery(id+"F12.opExtrude","SWEPT_BODY",BODY,{"disambiguationData":[OSD([sQuery(id+"F2.wireOp",EDGE,"E53"),sQuery(id+"F2.wireOp",EDGE,"E54"),sQuery(id+"F2.wireOp",EDGE,"E55.MirrorCS"),sQuery(id+"F2.wireOp",EDGE,"E56.MirrorCS"),sQuery(id+"F2.wireOp",EDGE,"E57.1.0"),sQuery(id+"F2.wireOp",EDGE,"E57.1.1"),sQuery(id+"F2.wireOp",EDGE,"E57.1.2"),sQuery(id+"F2.wireOp",EDGE,"E57.1.3"),sQuery(id+"F2.wireOp",EDGE,"E57.2.0"),sQuery(id+"F2.wireOp",EDGE,"E57.2.1"),sQuery(id+"F2.wireOp",EDGE,"E57.2.2"),sQuery(id+"F2.wireOp",EDGE,"E57.2.3"),sQuery(id+"F2.wireOp",EDGE,"E57.3.0"),sQuery(id+"F2.wireOp",EDGE,"E57.3.1"),sQuery(id+"F2.wireOp",EDGE,"E57.3.2"),sQuery(id+"F2.wireOp",EDGE,"E57.3.3"),sQuery(id+"F2.wireOp",EDGE,"E57.4.0"),sQuery(id+"F2.wireOp",EDGE,"E57.4.1"),sQuery(id+"F2.wireOp",EDGE,"E57.4.2"),sQuery(id+"F2.wireOp",EDGE,"E57.4.3"),sQuery(id+"F2.wireOp",EDGE,"E57.5.0"),sQuery(id+"F2.wireOp",EDGE,"E57.5.1"),sQuery(id+"F2.wireOp",EDGE,"E57.5.2"),sQuery(id+"F2.wireOp",EDGE,"E57.5.3"),sQuery(id+"F2.wireOp",EDGE,"E57.6.0"),sQuery(id+"F2.wireOp",EDGE,"E57.6.1"),sQuery(id+"F2.wireOp",EDGE,"E57.6.2"),sQuery(id+"F2.wireOp",EDGE,"E57.6.3"),sQuery(id+"F2.wireOp",EDGE,"E57.7.0"),sQuery(id+"F2.wireOp",EDGE,"E57.7.1"),sQuery(id+"F2.wireOp",EDGE,"E57.7.2"),sQuery(id+"F2.wireOp",EDGE,"E57.7.3"),sQuery(id+"F2.wireOp",EDGE,"E58"),sQuery(id+"F2.wireOp",EDGE,"E59"),sQuery(id+"F2.wireOp",EDGE,"E60"),sQuery(id+"F2.wireOp",EDGE,"E61"),sQuery(id+"F2.wireOp",EDGE,"E62"),sQuery(id+"F2.wireOp",EDGE,"E63.0"),sQuery(id+"F2.wireOp",EDGE,"E63.1"),sQuery(id+"F2.wireOp",EDGE,"E63.2"),sQuery(id+"F2.wireOp",EDGE,"E63.3"),sQuery(id+"F2.wireOp",EDGE,"E63.4"),sQuery(id+"F2.wireOp",EDGE,"E63.5"),sQuery(id+"F2.wireOp",EDGE,"E63.6"),sQuery(id+"F2.wireOp",EDGE,"E63.7"),sQuery(id+"F2.wireOp",EDGE,"E64.1.1"),sQuery(id+"F2.wireOp",EDGE,"E64.1.2"),sQuery(id+"F2.wireOp",EDGE,"E64.1.3"),sQuery(id+"F2.wireOp",EDGE,"E64.1.4"),sQuery(id+"F2.wireOp",EDGE,"E64.1.5"),sQuery(id+"F2.wireOp",EDGE,"E64.2.1"),sQuery(id+"F2.wireOp",EDGE,"E64.2.2"),sQuery(id+"F2.wireOp",EDGE,"E64.2.3"),sQuery(id+"F2.wireOp",EDGE,"E64.2.4"),sQuery(id+"F2.wireOp",EDGE,"E64.2.5"),sQuery(id+"F2.wireOp",EDGE,"E64.3.1"),sQuery(id+"F2.wireOp",EDGE,"E64.3.2"),sQuery(id+"F2.wireOp",EDGE,"E64.3.3"),sQuery(id+"F2.wireOp",EDGE,"E64.3.4"),sQuery(id+"F2.wireOp",EDGE,"E64.3.5"),sQuery(id+"F2.wireOp",EDGE,"E64.4.1"),sQuery(id+"F2.wireOp",EDGE,"E64.4.2"),sQuery(id+"F2.wireOp",EDGE,"E64.4.3"),sQuery(id+"F2.wireOp",EDGE,"E64.4.4"),sQuery(id+"F2.wireOp",EDGE,"E64.4.5"),sQuery(id+"F2.wireOp",EDGE,"E64.5.1"),sQuery(id+"F2.wireOp",EDGE,"E64.5.2"),sQuery(id+"F2.wireOp",EDGE,"E64.5.3"),sQuery(id+"F2.wireOp",EDGE,"E64.5.4"),sQuery(id+"F2.wireOp",EDGE,"E64.5.5"),sQuery(id+"F2.wireOp",EDGE,"E64.6.1"),sQuery(id+"F2.wireOp",EDGE,"E64.6.2"),sQuery(id+"F2.wireOp",EDGE,"E64.6.3"),sQuery(id+"F2.wireOp",EDGE,"E64.6.4"),sQuery(id+"F2.wireOp",EDGE,"E64.6.5"),sQuery(id+"F2.wireOp",EDGE,"E64.7.1"),sQuery(id+"F2.wireOp",EDGE,"E64.7.2"),sQuery(id+"F2.wireOp",EDGE,"E64.7.3"),sQuery(id+"F2.wireOp",EDGE,"E64.7.4"),sQuery(id+"F2.wireOp",EDGE,"E64.7.5")])]});
            var Q1;
            Q1=sQuery(id+"F8.wireOp",EDGE,"E124");
            transform(context, id + "F13", {"entities" : qUnion([Q0]), "transformType" : TransformType.ROTATION, "transformAxis" : qUnion([Q1]), "angle" : 90 * degree, "oppositeDirection" : true, "makeCopy" : false});
        }
        {
            var Q0;
            Q0 = qSketchRegion(id + "F3", true);
            extrude(context, id + "F14", {"entities" : qUnion([Q0]), "depth" : 100 * mm, "offsetDistance" : 25 * mm});
        }
        {
            var Q0;
            Q0=makeQuery(id+"F14.opExtrude","SWEPT_BODY",BODY,{"disambiguationData":[OSD([sQuery(id+"F3.wireOp",EDGE,"E65"),sQuery(id+"F3.wireOp",EDGE,"E66"),sQuery(id+"F3.wireOp",EDGE,"E67"),sQuery(id+"F3.wireOp",EDGE,"E68"),sQuery(id+"F3.wireOp",EDGE,"E69.MirrorCS"),sQuery(id+"F3.wireOp",EDGE,"E70.MirrorCS"),sQuery(id+"F3.wireOp",EDGE,"E71.MirrorCS"),sQuery(id+"F3.wireOp",EDGE,"E72.MirrorCS"),sQuery(id+"F3.wireOp",EDGE,"E73.2.0"),sQuery(id+"F3.wireOp",EDGE,"E73.2.1"),sQuery(id+"F3.wireOp",EDGE,"E73.2.2"),sQuery(id+"F3.wireOp",EDGE,"E73.2.3"),sQuery(id+"F3.wireOp",EDGE,"E73.2.4"),sQuery(id+"F3.wireOp",EDGE,"E73.2.5"),sQuery(id+"F3.wireOp",EDGE,"E73.2.6"),sQuery(id+"F3.wireOp",EDGE,"E73.2.7"),sQuery(id+"F3.wireOp",EDGE,"E73.4.0"),sQuery(id+"F3.wireOp",EDGE,"E73.4.1"),sQuery(id+"F3.wireOp",EDGE,"E73.4.2"),sQuery(id+"F3.wireOp",EDGE,"E73.4.3"),sQuery(id+"F3.wireOp",EDGE,"E73.4.4"),sQuery(id+"F3.wireOp",EDGE,"E73.4.5"),sQuery(id+"F3.wireOp",EDGE,"E73.4.6"),sQuery(id+"F3.wireOp",EDGE,"E73.4.7"),sQuery(id+"F3.wireOp",EDGE,"E73.6.0"),sQuery(id+"F3.wireOp",EDGE,"E73.6.1"),sQuery(id+"F3.wireOp",EDGE,"E73.6.2"),sQuery(id+"F3.wireOp",EDGE,"E73.6.3"),sQuery(id+"F3.wireOp",EDGE,"E73.6.4"),sQuery(id+"F3.wireOp",EDGE,"E73.6.5"),sQuery(id+"F3.wireOp",EDGE,"E73.6.6"),sQuery(id+"F3.wireOp",EDGE,"E73.6.7"),sQuery(id+"F3.wireOp",EDGE,"Ys2Be1Yr-EZaZ-nxLq-AtzW-NfP8CDdjYFig"),sQuery(id+"F3.wireOp",EDGE,"1WHCVvYJ-8DBw-rl3T-6VtR-tob8E4Ja1X87"),sQuery(id+"F3.wireOp",EDGE,"d58Mbq4g-Wgvj-9vxc-5tHB-IZwFOdAdUBL4"),sQuery(id+"F3.wireOp",EDGE,"SEezgCOG-RgvV-GsVs-zl9I-MNy84fX5w3ia"),sQuery(id+"F3.wireOp",EDGE,"BaMnu4i5-zKZn-dw3v-x8LB-4UwjnYtbGunT"),sQuery(id+"F3.wireOp",EDGE,"HxLmxDpU-Q6gV-Hnpi-mgEg-Zpml9xK8D1yl"),sQuery(id+"F3.wireOp",EDGE,"HUcnx0aX-zrAh-tRk6-wqms-4ZZxTPqEFQK1"),sQuery(id+"F3.wireOp",EDGE,"E74.2.0"),sQuery(id+"F3.wireOp",EDGE,"E74.2.1"),sQuery(id+"F3.wireOp",EDGE,"E74.2.2"),sQuery(id+"F3.wireOp",EDGE,"E74.2.3"),sQuery(id+"F3.wireOp",EDGE,"E74.2.4"),sQuery(id+"F3.wireOp",EDGE,"E74.2.5"),sQuery(id+"F3.wireOp",EDGE,"E74.2.6"),sQuery(id+"F3.wireOp",EDGE,"E74.4.0"),sQuery(id+"F3.wireOp",EDGE,"E74.4.1"),sQuery(id+"F3.wireOp",EDGE,"E74.4.2"),sQuery(id+"F3.wireOp",EDGE,"E74.4.3"),sQuery(id+"F3.wireOp",EDGE,"E74.4.4"),sQuery(id+"F3.wireOp",EDGE,"E74.4.5"),sQuery(id+"F3.wireOp",EDGE,"E74.4.6"),sQuery(id+"F3.wireOp",EDGE,"E74.6.0"),sQuery(id+"F3.wireOp",EDGE,"E74.6.1"),sQuery(id+"F3.wireOp",EDGE,"E74.6.2"),sQuery(id+"F3.wireOp",EDGE,"E74.6.3"),sQuery(id+"F3.wireOp",EDGE,"E74.6.4"),sQuery(id+"F3.wireOp",EDGE,"E74.6.5"),sQuery(id+"F3.wireOp",EDGE,"E74.6.6"),sQuery(id+"F3.wireOp",EDGE,"GqGdNSdP-mguD-0yzJ-s6cS-xtiWyyOyJmJY.bottom"),sQuery(id+"F3.wireOp",EDGE,"GqGdNSdP-mguD-0yzJ-s6cS-xtiWyyOyJmJY.top"),sQuery(id+"F3.wireOp",EDGE,"GqGdNSdP-mguD-0yzJ-s6cS-xtiWyyOyJmJY.left"),sQuery(id+"F3.wireOp",EDGE,"GqGdNSdP-mguD-0yzJ-s6cS-xtiWyyOyJmJY.right"),sQuery(id+"F3.wireOp",EDGE,"E75.bottom"),sQuery(id+"F3.wireOp",EDGE,"E75.top"),sQuery(id+"F3.wireOp",EDGE,"E75.left"),sQuery(id+"F3.wireOp",EDGE,"E75.right"),sQuery(id+"F3.wireOp",EDGE,"E76"),sQuery(id+"F3.wireOp",EDGE,"E77"),sQuery(id+"F3.wireOp",EDGE,"E79.MirrorCS"),sQuery(id+"F3.wireOp",EDGE,"E80.MirrorCS"),sQuery(id+"F3.wireOp",EDGE,"E81"),sQuery(id+"F3.wireOp",EDGE,"E82"),sQuery(id+"F3.wireOp",EDGE,"E83.MirrorCS"),sQuery(id+"F3.wireOp",EDGE,"E84.MirrorCS")])]});
            var Q1;
            Q1=sQuery(id+"F8.wireOp",EDGE,"E124");
            transform(context, id + "F15", {"entities" : qUnion([Q0]), "transformType" : TransformType.ROTATION, "transformAxis" : qUnion([Q1]), "angle" : 135 * degree, "oppositeDirection" : true, "makeCopy" : false});
        }
        {
            var Q0;
            Q0 = qSketchRegion(id + "F4", true);
            extrude(context, id + "F16", {"entities" : qUnion([Q0]), "depth" : 100 * mm, "offsetDistance" : 25 * mm});
        }
        {
            var Q0;
            Q0=makeQuery(id+"F16.opExtrude","SWEPT_BODY",BODY,{"disambiguationData":[OSD([sQuery(id+"F4.wireOp",EDGE,"E97"),sQuery(id+"F4.wireOp",EDGE,"E98"),sQuery(id+"F4.wireOp",EDGE,"E100"),sQuery(id+"F4.wireOp",EDGE,"E101.MirrorCS"),sQuery(id+"F4.wireOp",EDGE,"E102.MirrorCS"),sQuery(id+"F4.wireOp",EDGE,"E103.MirrorCS")])]});
            var Q1;
            Q1=sQuery(id+"F8.wireOp",EDGE,"E124");
            transform(context, id + "F17", {"entities" : qUnion([Q0]), "transformType" : TransformType.ROTATION, "transformAxis" : qUnion([Q1]), "angle" : 180 * degree, "oppositeDirection" : true, "makeCopy" : false});
        }
        {
            var Q0;
            Q0 = qSketchRegion(id + "F5", true);
            extrude(context, id + "F18", {"entities" : qUnion([Q0]), "depth" : 100 * mm, "offsetDistance" : 25 * mm});
        }
        {
            var Q0;
            Q0=makeQuery(id+"F18.opExtrude","SWEPT_BODY",BODY,{"disambiguationData":[OSD([sQuery(id+"F5.wireOp",EDGE,"E104"),sQuery(id+"F5.wireOp",EDGE,"E105")])]});
            var Q1;
            Q1=sQuery(id+"F8.wireOp",EDGE,"E124");
            transform(context, id + "F19", {"entities" : qUnion([Q0]), "transformType" : TransformType.ROTATION, "transformAxis" : qUnion([Q1]), "angle" : 225 * degree, "oppositeDirection" : true, "makeCopy" : false});
        }
        {
            var Q0;
            Q0 = qSketchRegion(id + "F7", true);
            extrude(context, id + "F20", {"entities" : qUnion([Q0]), "depth" : 100 * mm, "offsetDistance" : 25 * mm});
        }
        {
            var Q0;
            Q0=makeQuery(id+"F20.opExtrude","SWEPT_BODY",BODY,{"disambiguationData":[OSD([sQuery(id+"F7.wireOp",EDGE,"E111"),sQuery(id+"F7.wireOp",EDGE,"E112"),sQuery(id+"F7.wireOp",EDGE,"E113"),sQuery(id+"F7.wireOp",EDGE,"E114"),sQuery(id+"F7.wireOp",EDGE,"E115"),sQuery(id+"F7.wireOp",EDGE,"E116"),sQuery(id+"F7.wireOp",EDGE,"E117"),sQuery(id+"F7.wireOp",EDGE,"E118"),sQuery(id+"F7.wireOp",EDGE,"E119"),sQuery(id+"F7.wireOp",EDGE,"E120.0"),sQuery(id+"F7.wireOp",EDGE,"E120.1"),sQuery(id+"F7.wireOp",EDGE,"E120.2"),sQuery(id+"F7.wireOp",EDGE,"E120.3"),sQuery(id+"F7.wireOp",EDGE,"E120.4"),sQuery(id+"F7.wireOp",EDGE,"E120.5"),sQuery(id+"F7.wireOp",EDGE,"bXNJUFdC-X7KN-8fSR-jH2D-TLxbVt0VBxro")])]});
            var Q1;
            Q1=sQuery(id+"F8.wireOp",EDGE,"E124");
            transform(context, id + "F21", {"entities" : qUnion([Q0]), "transformType" : TransformType.ROTATION, "transformAxis" : qUnion([Q1]), "angle" : 315 * degree, "oppositeDirection" : true, "makeCopy" : false});
        }
        {
            var Q0;
            Q0 = qSketchRegion(id + "F6", true);
            extrude(context, id + "F22", {"entities" : qUnion([Q0]), "depth" : 100 * mm, "offsetDistance" : 25 * mm});
        }
        {
            var Q0;
            Q0=makeQuery(id+"F22.opExtrude","SWEPT_BODY",BODY,{"disambiguationData":[OSD([sQuery(id+"F6.wireOp",EDGE,"E107"),sQuery(id+"F6.wireOp",EDGE,"E108.MirrorCS"),sQuery(id+"F6.wireOp",EDGE,"0dcc21a1-5424-41e2-b2c9-b1d93b472560.0"),sQuery(id+"F6.wireOp",EDGE,"0dcc21a1-5424-41e2-b2c9-b1d93b472560.1")])]});
            var Q1;
            Q1=sQuery(id+"F8.wireOp",EDGE,"E124");
            transform(context, id + "F23", {"entities" : qUnion([Q0]), "transformType" : TransformType.ROTATION, "transformAxis" : qUnion([Q1]), "angle" : 270 * degree, "oppositeDirection" : true, "makeCopy" : false});
        }
        {
            var Q0;
            {var subQ0=sQuery(id+"F8.wireOp",EDGE,"E133");Q0=makeQuery(id+"F8.imprint","IMPRINT",FACE,{"disambiguationData":[TD([[makeQuery(id+"F8.imprint","IMPRINT",EDGE,{"derivedFrom":subQ0}),1.0]])]});}
            var Q1;
            {var subQ0=sQuery(id+"F8.wireOp",EDGE,"E135");Q1=makeQuery(id+"F8.imprint","IMPRINT",FACE,{"disambiguationData":[TD([[makeQuery(id+"F8.imprint","IMPRINT",EDGE,{"derivedFrom":subQ0}),1.0]])]});}
            var Q2;
            Q2=sQuery(id+"F8.wireOp",EDGE,"E124");
            revolve(context, id + "F24", {"entities" : qUnion([Q0, Q1]), "axis" : qUnion([Q2]), "revolveType" : RevolveType.FULL});
        }
        {
            var Q0;
            {var subQ6=sQuery(id+"F8.wireOp",EDGE,"E126");Q0=makeQuery(id+"F8.imprint","IMPRINT",FACE,{"disambiguationData":[TD([[makeQuery(id+"F8.imprint","IMPRINT",EDGE,{"derivedFrom":subQ6}),1.0]])]});}
            var Q1;
            {var subQ6=sQuery(id+"F8.wireOp",EDGE,"E130");Q1=makeQuery(id+"F8.imprint","IMPRINT",FACE,{"disambiguationData":[TD([[makeQuery(id+"F8.imprint","IMPRINT",EDGE,{"derivedFrom":subQ6}),-1.0]])]});}
            var Q2;
            Q2=sQuery(id+"F8.wireOp",EDGE,"E124");
            revolve(context, id + "F25", {"operationType" : NewBodyOperationType.REMOVE, "entities" : qUnion([Q0, Q1]), "axis" : qUnion([Q2]), "revolveType" : RevolveType.FULL, "oppositeDirection" : true});
        }
    });
